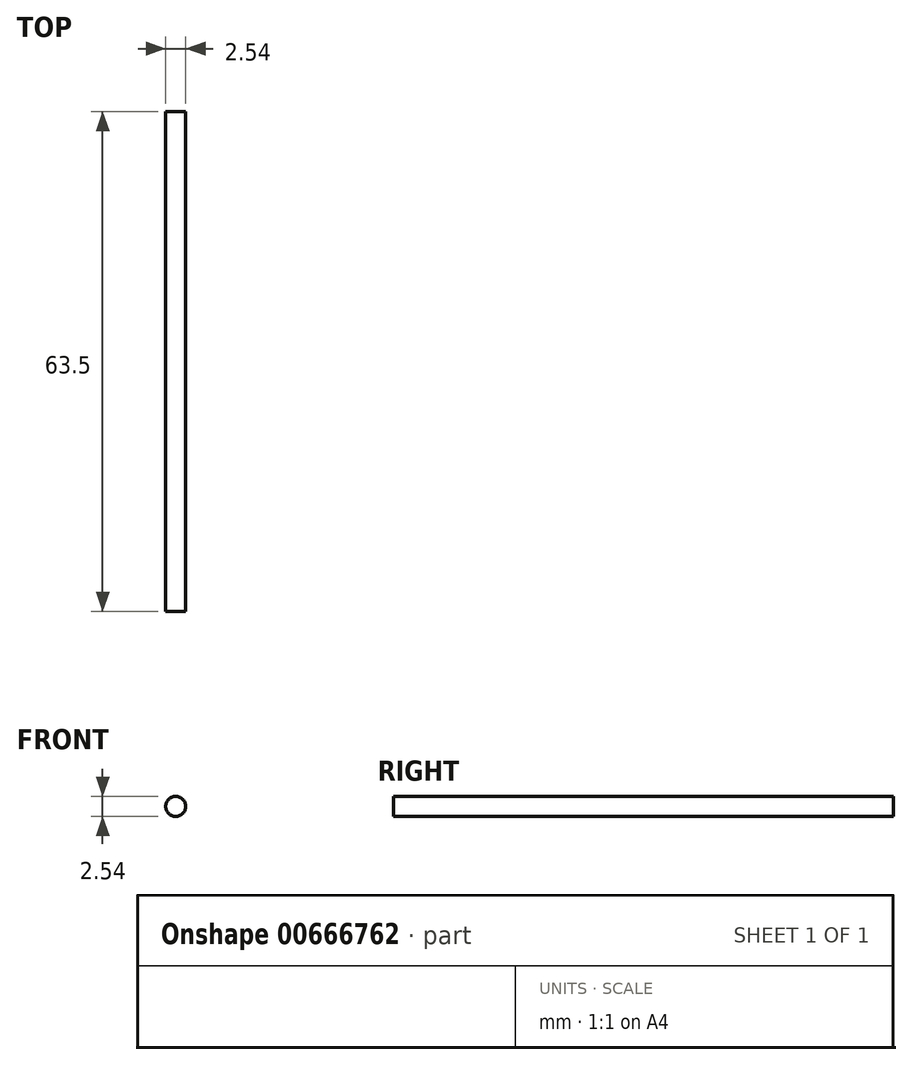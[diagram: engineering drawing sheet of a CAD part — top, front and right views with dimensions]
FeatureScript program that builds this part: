
annotation { "Feature Type Name" : "Feature", "Feature Type Description" : "" }
export const myFeature = defineFeature(function(context is Context, id is Id, definition is map)
    precondition{}
    {
        {
            var Q0;
            Q0=qCreatedBy(makeId("Front.planeOp"),FACE);
            var sketch = newSketch(context, id + "F0", { "sketchPlane" : qUnion([Q0])});
            skCircle(sketch, "E0", {"center": v(0, 0) * mm, "radius": 1.27 * mm});
            skSolve(sketch);
        }
        {
            var Q0;
            Q0 = qSketchRegion(id + "F0", true);
            extrude(context, id + "F1", {"entities" : qUnion([Q0]), "depth" : 63.5 * mm, "offsetDistance" : 25.4 * mm});
        }
    });
